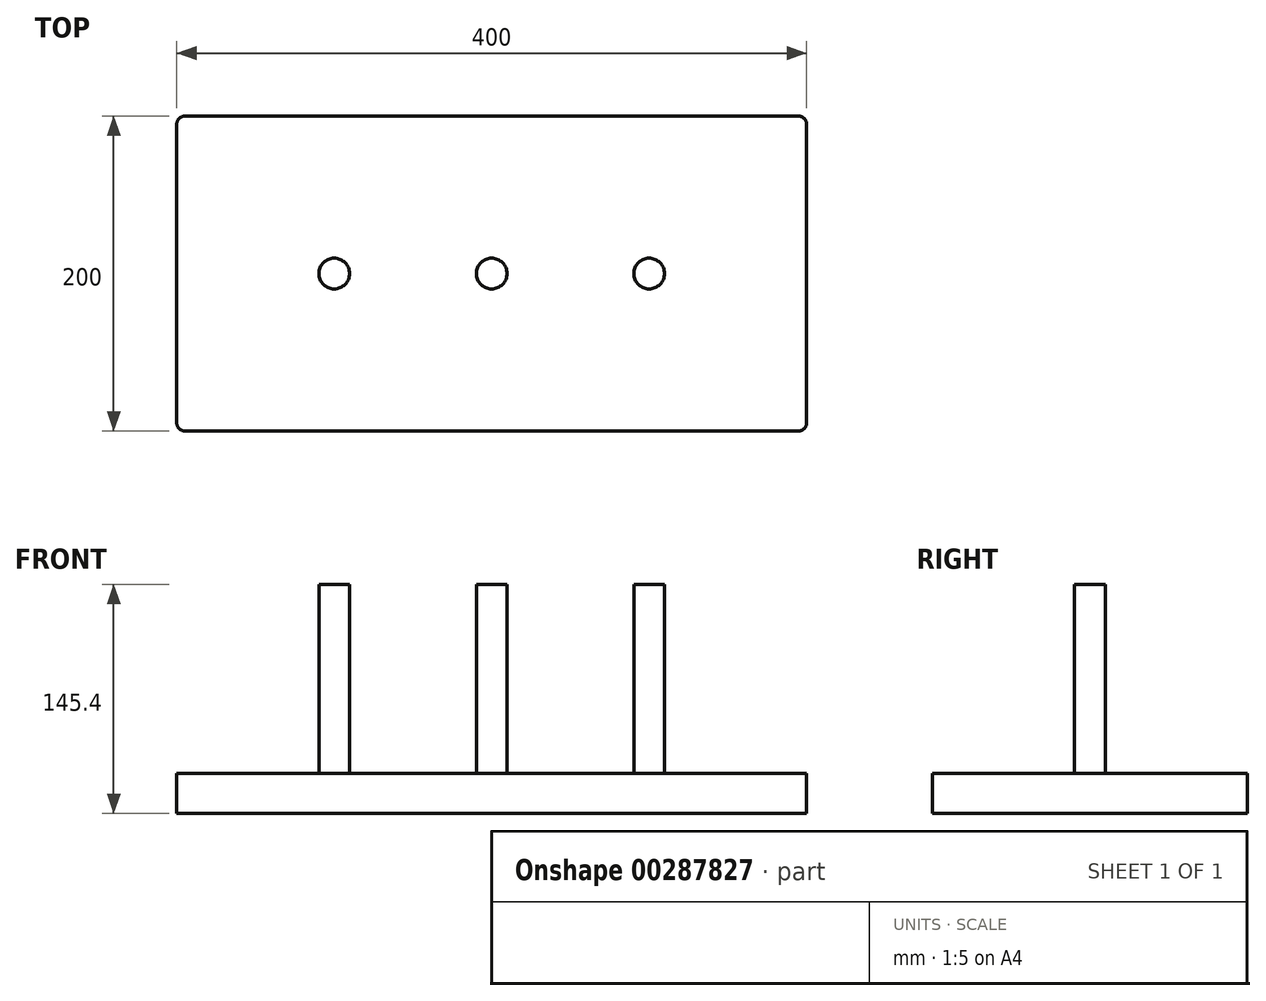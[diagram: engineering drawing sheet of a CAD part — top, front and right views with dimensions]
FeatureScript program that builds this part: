
annotation { "Feature Type Name" : "Feature", "Feature Type Description" : "" }
export const myFeature = defineFeature(function(context is Context, id is Id, definition is map)
    precondition{}
    {
        {
            var Q0;
            Q0=qCreatedBy(makeId("Top.planeOp"),FACE);
            var sketch = newSketch(context, id + "F0", { "sketchPlane" : qUnion([Q0])});
            skLineSegment(sketch, "E0.bottom", {"start": v(-200, 100) * mm, "end": v(200, 100) * mm});
            skLineSegment(sketch, "E0.top", {"start": v(-200, -100) * mm, "end": v(200, -100) * mm});
            skLineSegment(sketch, "E0.left", {"start": v(-200, 100) * mm, "end": v(-200, -100) * mm});
            skLineSegment(sketch, "E0.right", {"start": v(200, 100) * mm, "end": v(200, -100) * mm});
            skPoint(sketch, "E0.middle", {"position": v(0, 0) * mm});
            skSolve(sketch);
        }
        {
            var Q0;
            Q0=makeQuery(id+"F0.imprint","IMPRINT",FACE,{"disambiguationData":[TD([[makeQuery(id+"F0.imprint","IMPRINT",EDGE,{"derivedFrom":sQuery(id+"F0.wireOp",EDGE,"E0.bottom")}),-1.0]])]});
            extrude(context, id + "F1", {"entities" : qUnion([Q0]), "depth" : 25.4 * mm});
        }
        {
            var Q0;
            Q0=makeQuery(id+"F1.opExtrude","SWEPT_EDGE",EDGE,{"disambiguationData":[OSD([sQuery(id+"F0.wireOp",EDGE,"E0.bottom"),sQuery(id+"F0.wireOp",EDGE,"E0.right")])]});
            var Q1;
            Q1=makeQuery(id+"F1.opExtrude","SWEPT_EDGE",EDGE,{"disambiguationData":[OSD([sQuery(id+"F0.wireOp",EDGE,"E0.top"),sQuery(id+"F0.wireOp",EDGE,"E0.right")])]});
            var Q2;
            Q2=makeQuery(id+"F1.opExtrude","SWEPT_EDGE",EDGE,{"disambiguationData":[OSD([sQuery(id+"F0.wireOp",EDGE,"E0.bottom"),sQuery(id+"F0.wireOp",EDGE,"E0.left")])]});
            var Q3;
            Q3=makeQuery(id+"F1.opExtrude","SWEPT_EDGE",EDGE,{"disambiguationData":[OSD([sQuery(id+"F0.wireOp",EDGE,"E0.top"),sQuery(id+"F0.wireOp",EDGE,"E0.left")])]});
            fillet(context, id + "F2", {"entities" : qUnion([Q0, Q1, Q2, Q3]), "radius" : 5.08 * mm, "tangentPropagation" : true, "allowEdgeOverflow" : false});
        }
        {
            var Q0;
            Q0=makeQuery(id+"F1.opExtrude","CAP_FACE",FACE,{"disambiguationData":[OSD([sQuery(id+"F0.wireOp",EDGE,"E0.bottom"),sQuery(id+"F0.wireOp",EDGE,"E0.top"),sQuery(id+"F0.wireOp",EDGE,"E0.left"),sQuery(id+"F0.wireOp",EDGE,"E0.right")])],"isStart":false});
            var sketch = newSketch(context, id + "F3", { "sketchPlane" : qUnion([Q0])});
            skCircle(sketch, "E1", {"center": v(-100, 0) * mm, "radius": 9.75 * mm});
            skCircle(sketch, "E2", {"center": v(0, 0) * mm, "radius": 9.75 * mm});
            skCircle(sketch, "E3", {"center": v(100, 0) * mm, "radius": 9.75 * mm});
            skSolve(sketch);
        }
        {
            var Q0;
            Q0 = qSketchRegion(id + "F3", true);
            extrude(context, id + "F4", {"entities" : qUnion([Q0]), "operationType" : NewBodyOperationType.ADD, "depth" : 120 * mm});
        }
    });
